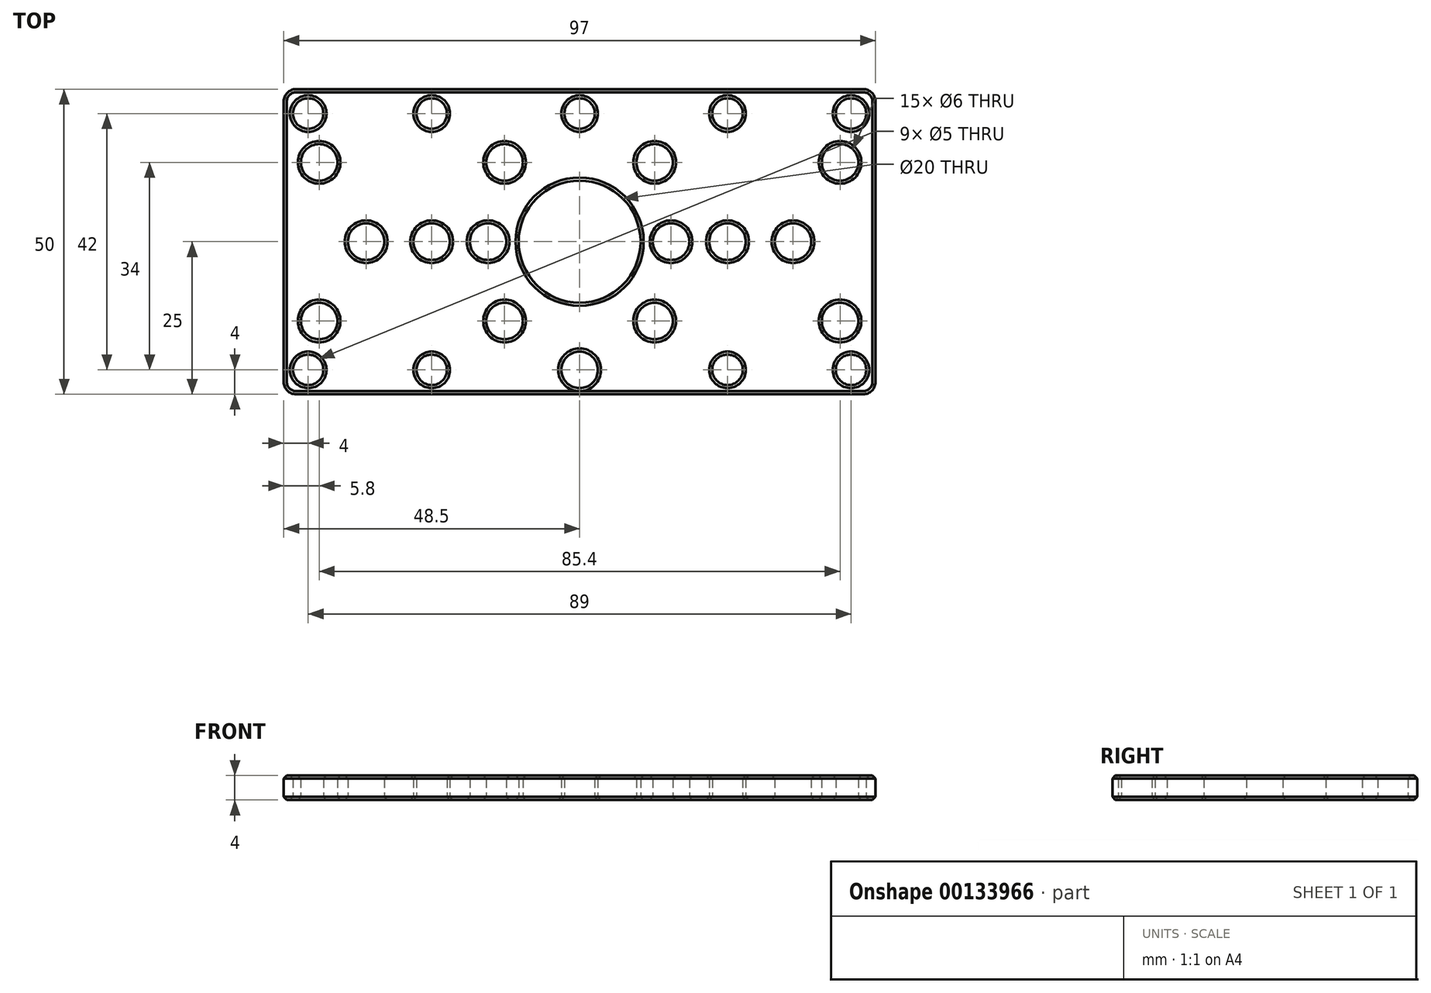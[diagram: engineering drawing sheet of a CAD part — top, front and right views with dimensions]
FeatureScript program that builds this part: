
annotation { "Feature Type Name" : "Feature", "Feature Type Description" : "" }
export const myFeature = defineFeature(function(context is Context, id is Id, definition is map)
    precondition{}
    {
        {
            var Q0;
            Q0=qCreatedBy(makeId("Top.planeOp"),FACE);
            var sketch = newSketch(context, id + "F0", { "sketchPlane" : qUnion([Q0])});
            skLineSegment(sketch, "E0.bottom", {"start": v(48.5, -25) * mm, "end": v(-48.5, -25) * mm});
            skLineSegment(sketch, "E0.top", {"start": v(48.5, 25) * mm, "end": v(-48.5, 25) * mm});
            skLineSegment(sketch, "E0.left", {"start": v(48.5, -25) * mm, "end": v(48.5, 25) * mm});
            skLineSegment(sketch, "E0.right", {"start": v(-48.5, -25) * mm, "end": v(-48.5, 25) * mm});
            skPoint(sketch, "E0.middle", {"position": v(0, 0) * mm});
            skCircle(sketch, "E1", {"center": v(0, 0) * mm, "radius": 10 * mm});
            skCircle(sketch, "E2", {"center": v(-42.7, 13) * mm, "radius": 3 * mm});
            skCircle(sketch, "E3", {"center": v(-12.3, 13) * mm, "radius": 3 * mm});
            skCircle(sketch, "E4", {"center": v(-42.7, -13) * mm, "radius": 3 * mm});
            skCircle(sketch, "E5", {"center": v(-12.3, -13) * mm, "radius": 3 * mm});
            skCircle(sketch, "E6", {"center": v(12.3, -13) * mm, "radius": 3 * mm});
            skCircle(sketch, "E7", {"center": v(42.7, -13) * mm, "radius": 3 * mm});
            skCircle(sketch, "E8", {"center": v(12.3, 13) * mm, "radius": 3 * mm});
            skCircle(sketch, "E9", {"center": v(42.7, 13) * mm, "radius": 3 * mm});
            skCircle(sketch, "E10", {"center": v(0, 21) * mm, "radius": 2.5 * mm});
            skPoint(sketch, "E10.centerSnap0", {"position": v(0, 25) * mm});
            skCircle(sketch, "E11", {"center": v(44.5, 21) * mm, "radius": 2.5 * mm});
            skCircle(sketch, "E12", {"center": v(-44.5, 21) * mm, "radius": 2.5 * mm});
            skCircle(sketch, "E13", {"center": v(44.5, -21) * mm, "radius": 2.5 * mm});
            skCircle(sketch, "E14", {"center": v(-44.5, -21) * mm, "radius": 2.5 * mm});
            skCircle(sketch, "E15", {"center": v(-24.25, 21) * mm, "radius": 2.5 * mm});
            skCircle(sketch, "E16", {"center": v(24.25, 21) * mm, "radius": 2.5 * mm});
            skCircle(sketch, "E17", {"center": v(-24.25, -21) * mm, "radius": 2.5 * mm});
            skCircle(sketch, "E18", {"center": v(24.25, -21) * mm, "radius": 2.5 * mm});
            skCircle(sketch, "E19", {"center": v(0, -21) * mm, "radius": 3 * mm});
            skCircle(sketch, "E20", {"center": v(-24.25, 0) * mm, "radius": 3 * mm});
            skCircle(sketch, "E21", {"center": v(24.25, 0) * mm, "radius": 3 * mm});
            skCircle(sketch, "E22", {"center": v(-35, 0) * mm, "radius": 3 * mm});
            skCircle(sketch, "E23", {"center": v(35, 0) * mm, "radius": 3 * mm});
            skCircle(sketch, "E24", {"center": v(-15, 0) * mm, "radius": 3 * mm});
            skCircle(sketch, "E25", {"center": v(15, 0) * mm, "radius": 3 * mm});
            skSolve(sketch);
        }
        {
            var Q0;
            Q0=qSketchRegion(id+"F0",true);
            extrude(context, id + "F1", {"entities" : qUnion([Q0]), "depth" : 4 * mm});
        }
        {
            var Q0;
            Q0=makeQuery(id+"F1.opExtrude","SWEPT_EDGE",EDGE,{"disambiguationData":[OSD([sQuery(id+"F0.wireOp",EDGE,"E0.top"),sQuery(id+"F0.wireOp",EDGE,"E0.right")])]});
            var Q1;
            Q1=makeQuery(id+"F1.opExtrude","SWEPT_EDGE",EDGE,{"disambiguationData":[OSD([sQuery(id+"F0.wireOp",EDGE,"E0.bottom"),sQuery(id+"F0.wireOp",EDGE,"E0.right")])]});
            var Q2;
            Q2=makeQuery(id+"F1.opExtrude","SWEPT_EDGE",EDGE,{"disambiguationData":[OSD([sQuery(id+"F0.wireOp",EDGE,"E0.bottom"),sQuery(id+"F0.wireOp",EDGE,"E0.left")])]});
            var Q3;
            Q3=makeQuery(id+"F1.opExtrude","SWEPT_EDGE",EDGE,{"disambiguationData":[OSD([sQuery(id+"F0.wireOp",EDGE,"E0.top"),sQuery(id+"F0.wireOp",EDGE,"E0.left")])]});
            fillet(context, id + "F2", {"entities" : qUnion([Q0, Q1, Q2, Q3]), "radius" : 2 * mm, "tangentPropagation" : true, "allowEdgeOverflow" : false});
        }
        {
            var Q0;
            Q0=makeQuery(id+"F1.opExtrude","CAP_FACE",FACE,{"disambiguationData":[OSD([sQuery(id+"F0.wireOp",EDGE,"E0.bottom"),sQuery(id+"F0.wireOp",EDGE,"E0.top"),sQuery(id+"F0.wireOp",EDGE,"E0.left"),sQuery(id+"F0.wireOp",EDGE,"E0.right"),sQuery(id+"F0.wireOp",EDGE,"E1"),sQuery(id+"F0.wireOp",EDGE,"E2"),sQuery(id+"F0.wireOp",EDGE,"E3"),sQuery(id+"F0.wireOp",EDGE,"E4"),sQuery(id+"F0.wireOp",EDGE,"E5"),sQuery(id+"F0.wireOp",EDGE,"E6"),sQuery(id+"F0.wireOp",EDGE,"E7"),sQuery(id+"F0.wireOp",EDGE,"E8"),sQuery(id+"F0.wireOp",EDGE,"E9"),sQuery(id+"F0.wireOp",EDGE,"JYlAmVR4-Q9DO-m8nX-R6dD-j7H3OKJ7AEJS"),sQuery(id+"F0.wireOp",EDGE,"970X8EOb-Kf75-NLyP-bxgz-0VRt3XqA3mbQ"),sQuery(id+"F0.wireOp",EDGE,"E10"),sQuery(id+"F0.wireOp",EDGE,"E11"),sQuery(id+"F0.wireOp",EDGE,"E12"),sQuery(id+"F0.wireOp",EDGE,"E13"),sQuery(id+"F0.wireOp",EDGE,"E14")])],"isStart":false});
            var Q1;
            Q1=makeQuery(id+"F1.opExtrude","CAP_FACE",FACE,{"disambiguationData":[OSD([sQuery(id+"F0.wireOp",EDGE,"E0.bottom"),sQuery(id+"F0.wireOp",EDGE,"E0.top"),sQuery(id+"F0.wireOp",EDGE,"E0.left"),sQuery(id+"F0.wireOp",EDGE,"E0.right"),sQuery(id+"F0.wireOp",EDGE,"E1"),sQuery(id+"F0.wireOp",EDGE,"E2"),sQuery(id+"F0.wireOp",EDGE,"E3"),sQuery(id+"F0.wireOp",EDGE,"E4"),sQuery(id+"F0.wireOp",EDGE,"E5"),sQuery(id+"F0.wireOp",EDGE,"E6"),sQuery(id+"F0.wireOp",EDGE,"E7"),sQuery(id+"F0.wireOp",EDGE,"E8"),sQuery(id+"F0.wireOp",EDGE,"E9"),sQuery(id+"F0.wireOp",EDGE,"JYlAmVR4-Q9DO-m8nX-R6dD-j7H3OKJ7AEJS"),sQuery(id+"F0.wireOp",EDGE,"970X8EOb-Kf75-NLyP-bxgz-0VRt3XqA3mbQ"),sQuery(id+"F0.wireOp",EDGE,"E10"),sQuery(id+"F0.wireOp",EDGE,"E11"),sQuery(id+"F0.wireOp",EDGE,"E12"),sQuery(id+"F0.wireOp",EDGE,"E13"),sQuery(id+"F0.wireOp",EDGE,"E14")])],"isStart":true});
            chamfer(context, id + "F3", {"entities" : qUnion([Q0, Q1]), "width" : 0.5 * mm, "tangentPropagation" : true});
        }
    });
